# Revit family: Wood Wool - Ceiling Clouds
name_source: partatom
category: Specialty Equipment
units: mm (PartAtom-declared; Revit-internal decimal feet)

## family parameters
Always vertical = No
Cut with Voids When Loaded = No
Enable Cutting in Views = Yes
Maintain Annotation Orientation = No
OmniClass Number = 23.35.00.00
OmniClass Title = Covering, Cladding, and Finishes
Part Type = Normal
Room Calculation Point = No
Round Connector Dimension = Use Diameter
Shared = No
Work Plane-Based = Yes

## types (24) — shared parameters
Acoustics - NRC = Sound absorption varies from NRC 0.45 to 0.95 based on installation method used when tested per ASTM C423.
Assembly Code = C30
Default Elevation = 0' - 0"
Description = Acoustic Panels
Fire Rating = ASTM E84 - Class A
Manufacturer = Acoustical Surfaces, Inc.
Material = Envirocoustic Wood Wool
Model = Envirocoustic Wood Wool
Recycled Content Percentage = 0%
Type Comments = Acoustic panels
URL = https://www.acousticalsurfaces.com
Width = 2' - 0"

## per-type parameters (varying)
| type | Edge Option | Finish | Length | T | Thickness Options | ‍      1. Thickness 1-3/8" | ‍      2. Thickness 2" | ‍     1. Beveled | ‍     2. Square |
| 1-3/8" Square 2ft x 8ft Custom Painted | 2 | Paint - Acoustical-Surfaces - Custom Painted | 8' - 0" | 0' - 1 1/2" | 1 | Yes | No | No | Yes |
| 1-3/8" Square 2ft x 4ft Custom Painted | 2 | Paint - Acoustical-Surfaces - Custom Painted | 4' - 0" | 0' - 1 1/2" | 1 | Yes | No | No | Yes |
| 1-3/8" Square 2ft x 8ft Primed White | 2 | Paint - Acoustical-Surfaces - Primed White | 8' - 0" | 0' - 1 1/2" | 1 | Yes | No | No | Yes |
| 1-3/8" Square 2ft x 4ft Primed White | 2 | Paint - Acoustical-Surfaces - Primed White | 4' - 0" | 0' - 1 1/2" | 1 | Yes | No | No | Yes |
| 1-3/8" Square 2ft x 8ft Primed Clear | 2 | Paint - Acoustical-Surfaces - Primed Clear | 8' - 0" | 0' - 1 1/2" | 1 | Yes | No | No | Yes |
| 1-3/8" Square 2ft x 4ft Primed Clear | 2 | Paint - Acoustical-Surfaces - Primed Clear | 4' - 0" | 0' - 1 1/2" | 1 | Yes | No | No | Yes |
| 1-3/8" Beveled 2ft x 8ft Custom Painted | 1 | Paint - Acoustical-Surfaces - Custom Painted | 8' - 0" | 0' - 1 1/2" | 1 | Yes | No | Yes | No |
| 1-3/8" Beveled 2ft x 4ft Custom Painted | 1 | Paint - Acoustical-Surfaces - Custom Painted | 4' - 0" | 0' - 1 1/2" | 1 | Yes | No | Yes | No |
| 1-3/8" Beveled 2ft x 8ft Primed White | 1 | Paint - Acoustical-Surfaces - Primed White | 8' - 0" | 0' - 1 1/2" | 1 | Yes | No | Yes | No |
| 1-3/8" Beveled 2ft x 4ft Primed White | 1 | Paint - Acoustical-Surfaces - Primed White | 4' - 0" | 0' - 2" | 2 | No | Yes | Yes | No |
| 1-3/8" Beveled 2ft x 8ft Primed Clear | 1 | Paint - Acoustical-Surfaces - Primed Clear | 8' - 0" | 0' - 1 1/2" | 1 | Yes | No | Yes | No |
| 1-3/8" Beveled 2ft x 4ft Primed Clear | 1 | Paint - Acoustical-Surfaces - Primed Clear | 4' - 0" | 0' - 1 1/2" | 1 | Yes | No | Yes | No |
| 2" Beveled 2ft x 4ft Primed Clear | 1 | Paint - Acoustical-Surfaces - Primed Clear | 4' - 0" | 0' - 2" | 2 | No | Yes | Yes | No |
| 2" Beveled 2ft x 8ft Primed Clear | 1 | Paint - Acoustical-Surfaces - Primed Clear | 8' - 0" | 0' - 2" | 2 | No | Yes | Yes | No |
| 2" Beveled 2ft x 4ft Primed White | 1 | Paint - Acoustical-Surfaces - Primed White | 4' - 0" | 0' - 2" | 2 | No | Yes | Yes | No |
| 2" Beveled 2ft x 8ft Primed White | 1 | Paint - Acoustical-Surfaces - Primed White | 8' - 0" | 0' - 2" | 2 | No | Yes | Yes | No |
| 2" Beveled 2ft x 4ft Custom Painted | 1 | Paint - Acoustical-Surfaces - Custom Painted | 4' - 0" | 0' - 2" | 2 | No | Yes | Yes | No |
| 2" Beveled 2ft x 8ft Custom Painted | 1 | Paint - Acoustical-Surfaces - Custom Painted | 8' - 0" | 0' - 2" | 2 | No | Yes | Yes | No |
| 2" Square 2ft x 4ft Primed Clear | 2 | Paint - Acoustical-Surfaces - Primed Clear | 4' - 0" | 0' - 2" | 2 | No | Yes | No | Yes |
| 2" Square 2ft x 8ft Primed Clear | 2 | Paint - Acoustical-Surfaces - Primed Clear | 8' - 0" | 0' - 2" | 2 | No | Yes | No | Yes |
| 2" Square 2ft x 4ft Primed White | 2 | Paint - Acoustical-Surfaces - Primed White | 4' - 0" | 0' - 2" | 2 | No | Yes | No | Yes |
| 2" Square 2ft x 8ft Primed White | 2 | Paint - Acoustical-Surfaces - Primed White | 8' - 0" | 0' - 2" | 2 | No | Yes | No | Yes |
| 2" Square 2ft x 4ft Custom Painted | 2 | Paint - Acoustical-Surfaces - Custom Painted | 4' - 0" | 0' - 2" | 2 | No | Yes | No | Yes |
| 2" Square 2ft x 8ft Custom Painted | 2 | Paint - Acoustical-Surfaces - Custom Painted | 8' - 0" | 0' - 2" | 2 | No | Yes | No | Yes |

## geometry (parser evidence)
native form markers: Sweep x10
no freeform markers — native parametric forms only
